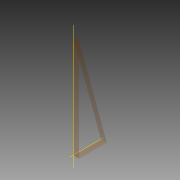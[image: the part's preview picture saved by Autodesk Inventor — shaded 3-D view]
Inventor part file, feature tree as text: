
AUTODESK INVENTOR PART (.ipt)
format: ipt  version: 2015 (Build 190159000, 159)  size: 68,608 bytes
history: native  units: mm
features: sketch x1, other x1, extrude x1
ambient origin geometry x8: Origin, YZ Plane, XZ Plane, XY Plane, X Axis, Y Axis, Z Axis, Center Point
bodies: Body1 (feature_tree)
feature tree (3):
  sketch  "Sketch1"  dims[d0=190.0mm d1=700.0mm d2=40.0mm d3=0.0mm]
  other  "Srf1"
  extrude  "ExtrusionSrf1"  Depth=700.0mm
